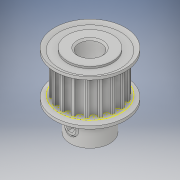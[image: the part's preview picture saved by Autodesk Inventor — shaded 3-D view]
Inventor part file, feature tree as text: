
AUTODESK INVENTOR PART (.ipt)
format: ipt  version: 2019.2 (Build 232265000, 265)  size: 405,504 bytes
history: native  units: mm
features: move_body x2, sketch x1, imported_body x1
ambient origin geometry x8: Origin, YZ Plane, XZ Plane, XY Plane, X Axis, Y Axis, Z Axis, Center Point
bodies: Solid1 (feature_tree)
feature tree (4):
  move_body  "Move Body1"
  move_body  "Move Body2"
  sketch  "Sketch1"  dims[d0=90.0deg d1=-15.707963mm]
  imported_body  "Base1"
